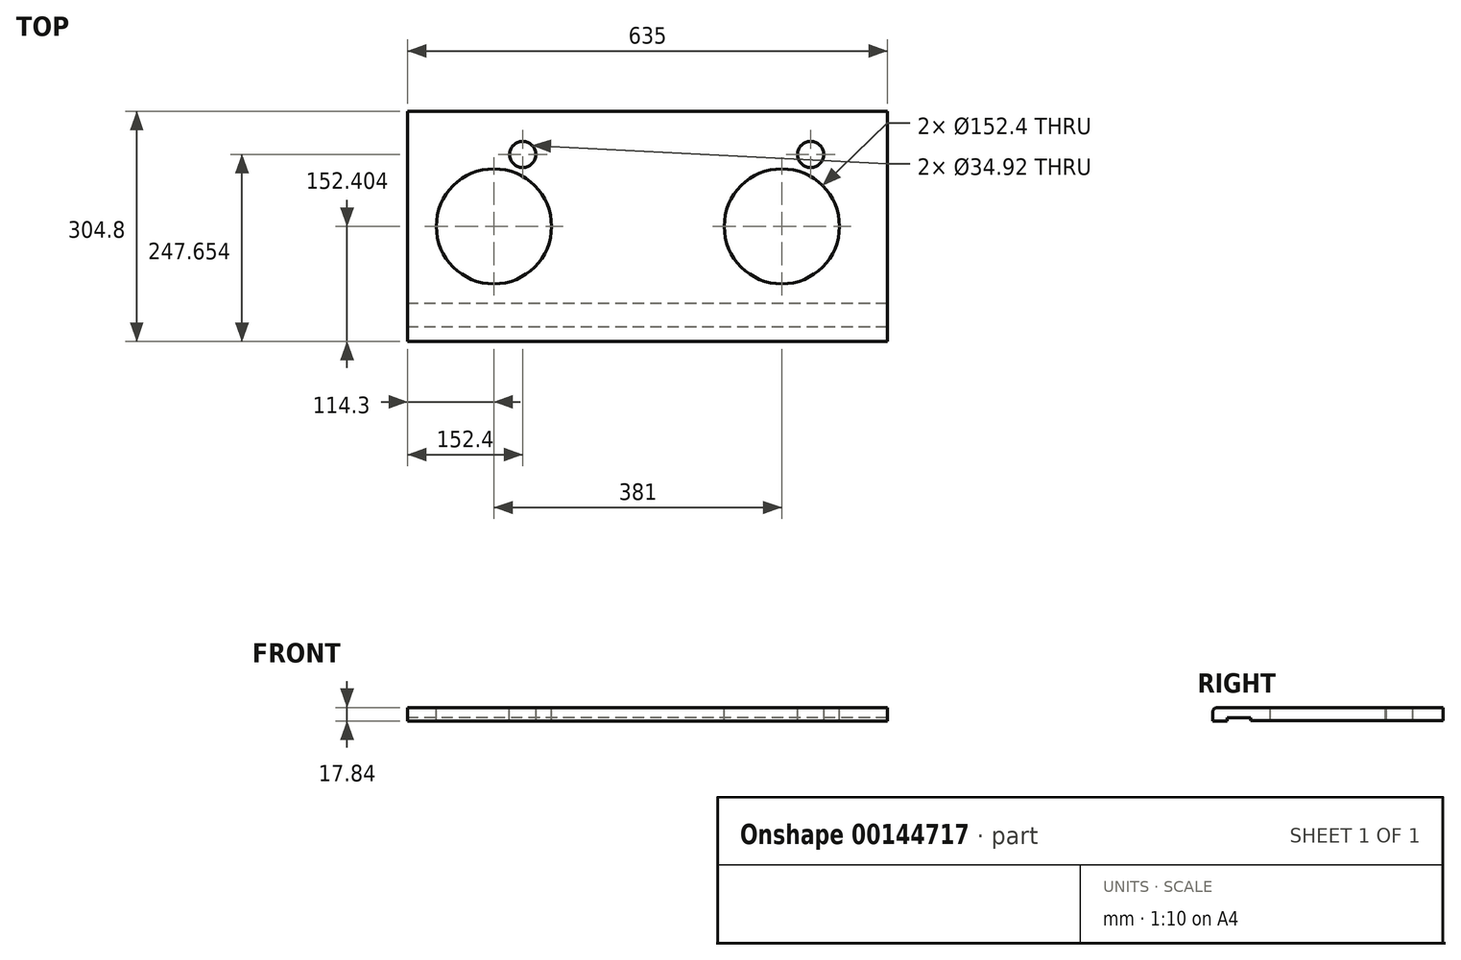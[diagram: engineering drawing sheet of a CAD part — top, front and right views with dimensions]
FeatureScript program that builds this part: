
annotation { "Feature Type Name" : "Feature", "Feature Type Description" : "" }
export const myFeature = defineFeature(function(context is Context, id is Id, definition is map)
    precondition{}
    {
        {
            var Q0;
            Q0=qCreatedBy(makeId("Right.planeOp"),FACE);
            var sketch = newSketch(context, id + "F0", { "sketchPlane" : qUnion([Q0])});
            skLineSegment(sketch, "E0", {"start": v(-9.4, 6.88) * mm, "end": v(-9.4, -4.6) * mm});
            skLineSegment(sketch, "E1", {"start": v(-9.4, -4.6) * mm, "end": v(9.65, -4.6) * mm});
            skLineSegment(sketch, "E2", {"start": v(9.65, -4.6) * mm, "end": v(9.65, 0) * mm});
            skLineSegment(sketch, "E3", {"start": v(9.65, 0) * mm, "end": v(40.86, 0) * mm});
            skLineSegment(sketch, "E4", {"start": v(295.4, -4.28) * mm, "end": v(295.4, 13.23) * mm});
            skLineSegment(sketch, "E5", {"start": v(295.4, 13.23) * mm, "end": v(-3.05, 13.23) * mm});
            skPoint(sketch, "E6.visualSharp", {"position": v(-9.4, 13.23) * mm});
            skArc(sketch, "E6.filletArc", {"start": v(-3.05, 13.23) * mm, "mid": v(-7.54, 11.37) * mm, "end": v(-9.4, 6.88) * mm});
            skLineSegment(sketch, "E7", {"start": v(40.86, 0) * mm, "end": v(40.86, -4.28) * mm});
            skLineSegment(sketch, "E8", {"start": v(40.86, -4.28) * mm, "end": v(295.4, -4.28) * mm});
            skPoint(sketch, "E9.orphan", {"position": v(295.4, 0) * mm});
            skSolve(sketch);
        }
        {
            var Q0;
            Q0=makeQuery(id+"F0.imprint","IMPRINT",FACE,{"disambiguationData":[TD([[makeQuery(id+"F0.imprint","IMPRINT",EDGE,{"derivedFrom":sQuery(id+"F0.wireOp",EDGE,"E0")}),1.0]])]});
            extrude(context, id + "F1", {"entities" : qUnion([Q0]), "depth" : 635 * mm});
        }
        {
            var Q0;
            Q0=makeQuery(id+"F1.opExtrude","SWEPT_FACE",FACE,{"disambiguationData":[OSD([sQuery(id+"F0.wireOp",EDGE,"E5")])]});
            var sketch = newSketch(context, id + "F2", { "sketchPlane" : qUnion([Q0])});
            skCircle(sketch, "E10", {"center": v(152.4, 238.25) * mm, "radius": 17.46 * mm});
            skCircle(sketch, "E11", {"center": v(533.4, 238.25) * mm, "radius": 17.46 * mm});
            skCircle(sketch, "E12", {"center": v(114.3, 143) * mm, "radius": 76.2 * mm});
            skCircle(sketch, "E13", {"center": v(495.3, 143) * mm, "radius": 76.2 * mm});
            skSolve(sketch);
        }
        {
            var Q0;
            Q0=makeQuery(id+"F2.imprint","IMPRINT",FACE,{"disambiguationData":[TD([[makeQuery(id+"F2.imprint","IMPRINT",EDGE,{"derivedFrom":sQuery(id+"F2.wireOp",EDGE,"E12")}),1.0]])]});
            var Q1;
            Q1=makeQuery(id+"F2.imprint","IMPRINT",FACE,{"disambiguationData":[TD([[makeQuery(id+"F2.imprint","IMPRINT",EDGE,{"derivedFrom":sQuery(id+"F2.wireOp",EDGE,"E13")}),1.0]])]});
            var Q2;
            Q2=makeQuery(id+"F2.imprint","IMPRINT",FACE,{"disambiguationData":[TD([[makeQuery(id+"F2.imprint","IMPRINT",EDGE,{"derivedFrom":sQuery(id+"F2.wireOp",EDGE,"E11")}),1.0]])]});
            var Q3;
            Q3=makeQuery(id+"F2.imprint","IMPRINT",FACE,{"disambiguationData":[TD([[makeQuery(id+"F2.imprint","IMPRINT",EDGE,{"derivedFrom":sQuery(id+"F2.wireOp",EDGE,"E10")}),1.0]])]});
            extrude(context, id + "F3", {"entities" : qUnion([Q0, Q1, Q2, Q3]), "operationType" : NewBodyOperationType.REMOVE, "oppositeDirection" : true, "depth" : 25.4 * mm});
        }
    });
